# Revit family: Legrand-Ups-Keor_HPE-60_300kVA
name_source: partatom
category: Installations électriques
revit_build: Autodesk Revit 2018 (Build: 20170223_1515(x64)
units: mm (PartAtom-declared; Revit-internal decimal feet)

## family parameters
Basée sur le plan de construction = Non
Conserver l'orientation des annotations = Non
Cote de connecteur circulaire = Utiliser le diamètre
Couper avec des vides une fois chargée = Non
Numéro OmniClass = 23.80.10.17.34
Partagée = Non
Point de calcul de pièce = Non
Titre OmniClass = Static Uninterruptible Power Supplies
Toujours verticalement = Oui
Type d'élément = Normal

## types (10) — shared parameters
Back Clearance = 50 mm  [stored 0.164042 ft]
Conductors = Cables
Connection constraint = Ahead and bottom
Connection constraint (signal) = Ahead and above/bottom
Fabricant = LEGRAND
Frequency of use = 50 Hz or 60 Hz selectable
Front Clearance = 1200 mm
General Conditions of Use = https://export.legrand.com
Humidity = 0-95% not condensing
Input / Output phase configuration = 3ph+N+PE/3ph+N+PE
Installation type = On the floor
Max sound pressure level = < 60 dB at 1m
Modèle = KEOR HP
Operating altitude = up to 1000 m altitude without derating
Operating temperature = from 0°C to +40°C
Output Voltage = 380,400,415 Vac
Output power factor = 1
Side Clearance = 600 mm
URL = https://ups.legrand.com
Visibilità aree d'installazione = Oui

## per-type parameters (varying)
| type | Active power of use | Cabinet Depth | Cabinet Height | Cabinet Width | Installation space | Nominal Power | Weight |
| 960565 | 60 kW | 940 mm  [stored 3.08399 ft] | 1800 mm  [stored 5.90551 ft] | 560 mm  [stored 1.83727 ft] | 0.9 m³ | 60 kVA | 250.0 kg |
| 960566 | 60 kW | 940 mm  [stored 3.08399 ft] | 1800 mm  [stored 5.90551 ft] | 560 mm  [stored 1.83727 ft] | 0.9 m³ | 60 kVA | 800.0 kg |
| 960567 | 80 kW | 940 mm  [stored 3.08399 ft] | 1800 mm  [stored 5.90551 ft] | 560 mm  [stored 1.83727 ft] | 0.9 m³ | 80 kVA | 300.0 kg |
| 960568 | 80 kW | 940 mm  [stored 3.08399 ft] | 1800 mm  [stored 5.90551 ft] | 560 mm  [stored 1.83727 ft] | 0.9 m³ | 80 kVA | 850.0 kg |
| 960569 | 100 kW | 940 mm  [stored 3.08399 ft] | 1800 mm  [stored 5.90551 ft] | 560 mm  [stored 1.83727 ft] | 0.9 m³ | 100 kVA | 320.0 kg |
| 960570 | 125 kW | 940 mm  [stored 3.08399 ft] | 1800 mm  [stored 5.90551 ft] | 560 mm  [stored 1.83727 ft] | 0.9 m³ | 125 kVA | 360.0 kg |
| 960571 | 160 kW | 940 mm  [stored 3.08399 ft] | 1800 mm  [stored 5.90551 ft] | 560 mm  [stored 1.83727 ft] | 0.9 m³ | 160 kVA | 380.0 kg |
| 960572 | 200 kW | 966 mm | 1976 mm | 880 mm  [stored 2.88714 ft] | 1.6 m³ | 200 kVA | 720.0 kg |
| 953500 | 250 kW | 966 mm | 1976 mm | 880 mm  [stored 2.88714 ft] | 1.6 m³ | 250 kVA | 850.0 kg |
| 953501 | 300 kW | 966 mm | 1976 mm | 880 mm  [stored 2.88714 ft] | 1.6 m³ | 300 kVA | 900.0 kg |

note: [stored X ft] marks values corroborated as IEEE doubles in the binary element streams (Revit-internal decimal feet)
